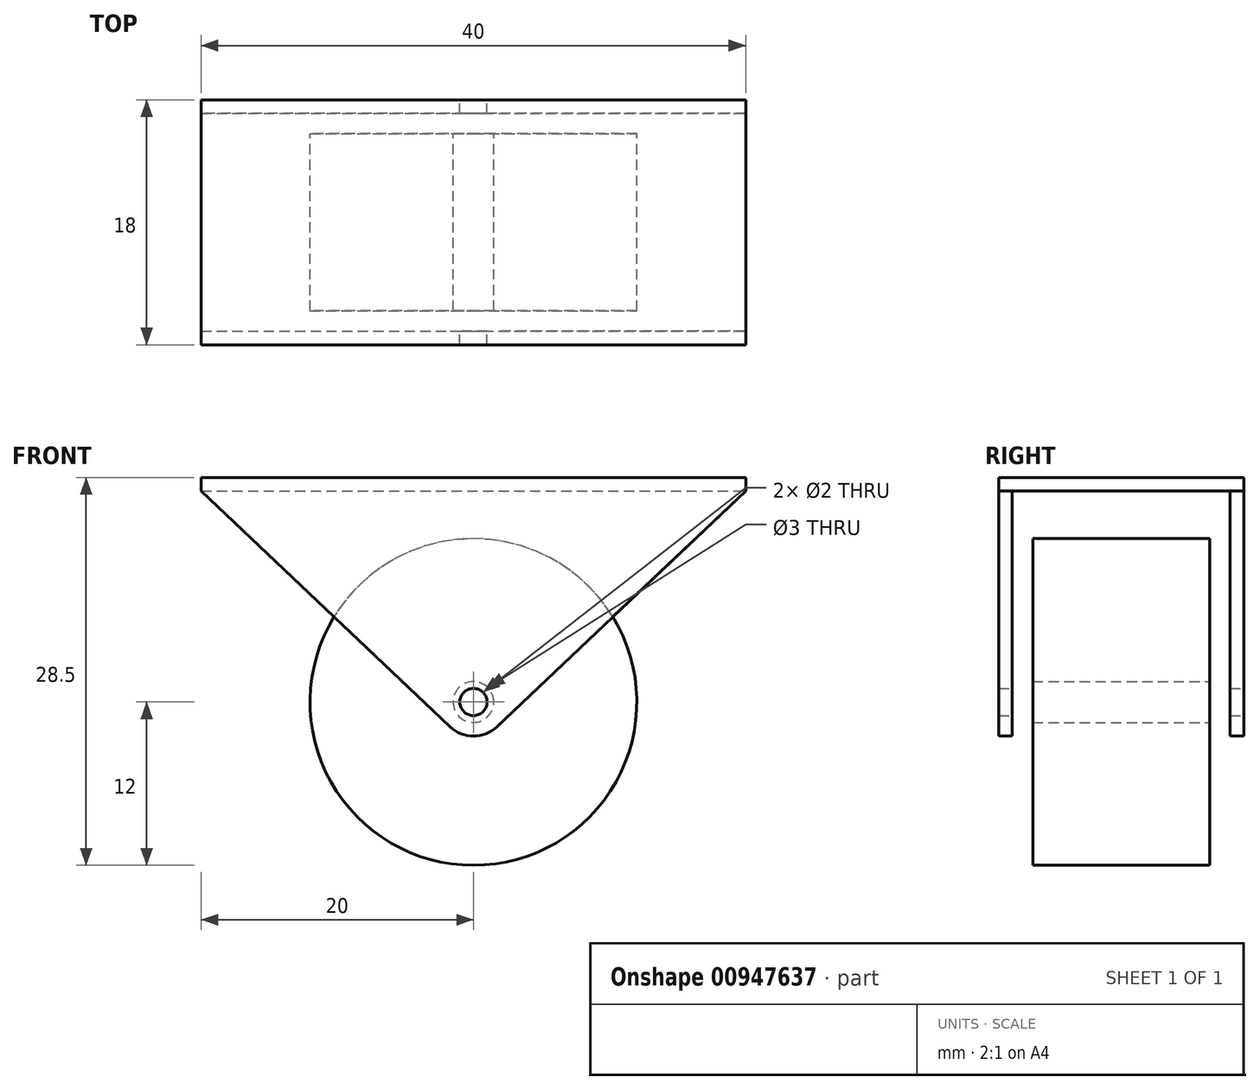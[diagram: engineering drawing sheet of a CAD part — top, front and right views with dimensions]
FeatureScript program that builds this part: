
annotation { "Feature Type Name" : "Feature", "Feature Type Description" : "" }
export const myFeature = defineFeature(function(context is Context, id is Id, definition is map)
    precondition{}
    {
        {
            var Q0;
            Q0=qCreatedBy(makeId("Front.planeOp"),FACE);
            var sketch = newSketch(context, id + "F0", { "sketchPlane" : qUnion([Q0])});
            skCircle(sketch, "E0", {"center": v(0, 0) * mm, "radius": 12 * mm});
            skCircle(sketch, "E1", {"center": v(0, 0) * mm, "radius": 1.5 * mm});
            skSolve(sketch);
        }
        {
            var Q0;
            Q0 = qSketchRegion(id + "F0", true);
            extrude(context, id + "F1", {"entities" : qUnion([Q0]), "depth" : 6.5 * mm, "offsetDistance" : 25 * mm, "hasSecondDirection" : true, "secondDirectionOppositeDirection" : true, "secondDirectionDepth" : 6.5 * mm});
        }
        {
            var Q0;
            Q0=qCreatedBy(makeId("Top.planeOp"),FACE);
            cPlane(context, id + "F2", {"entities" : qUnion([Q0]), "cplaneType" : CPlaneType.OFFSET, "offset" : (28 - 11.5) * mm, "width" : 150 * mm, "height" : 150 * mm});
        }
        {
            var Q0;
            Q0=qCreatedBy(id+"F2.planeOp",FACE);
            var sketch = newSketch(context, id + "F3", { "sketchPlane" : qUnion([Q0])});
            skLineSegment(sketch, "E2.bottom", {"start": v(-20, 9) * mm, "end": v(20, 9) * mm});
            skLineSegment(sketch, "E2.top", {"start": v(-20, -9) * mm, "end": v(20, -9) * mm});
            skLineSegment(sketch, "E2.left", {"start": v(-20, 9) * mm, "end": v(-20, -9) * mm});
            skLineSegment(sketch, "E2.right", {"start": v(20, 9) * mm, "end": v(20, -9) * mm});
            skPoint(sketch, "E3", {"position": v(-20, 0) * mm});
            skPoint(sketch, "E4", {"position": v(0, -9) * mm});
            skSolve(sketch);
        }
        {
            var Q0;
            Q0 = qSketchRegion(id + "F3", true);
            extrude(context, id + "F4", {"entities" : qUnion([Q0]), "oppositeDirection" : true, "depth" : 1 * mm, "offsetDistance" : 25 * mm});
        }
        {
            var Q0;
            Q0=makeQuery(id+"F4.opExtrude","SWEPT_FACE",FACE,{"disambiguationData":[OSD([sQuery(id+"F3.wireOp",EDGE,"E2.top")])]});
            var sketch = newSketch(context, id + "F5", { "sketchPlane" : qUnion([Q0])});
            skCircle(sketch, "E5", {"center": v(0, 0) * mm, "radius": 2.5 * mm});
            skLineSegment(sketch, "E6", {"start": v(-20, 15.5) * mm, "end": v(-1.72, -1.82) * mm});
            skLineSegment(sketch, "E7", {"start": v(20, 15.5) * mm, "end": v(1.72, -1.82) * mm});
            skSolve(sketch);
        }
        {
            var Q0;
            {var subQ0=sQuery(id+"F5.wireOp",EDGE,"E6");Q0=makeQuery(id+"F5.imprint","IMPRINT",FACE,{"disambiguationData":[TD([[makeQuery(id+"F5.imprint","IMPRINT",EDGE,{"derivedFrom":subQ0}),1.0]])]});}
            var Q1;
            {var subQ0=sQuery(id+"F5.wireOp",EDGE,"E5");var subQ1=makeQuery(id+"F5.imprint","INTERSECT",VERTEX,{"derivedFrom":[subQ0,sQuery(id+"F5.wireOp",EDGE,"E6")]});Q1=makeQuery(id+"F5.imprint","IMPRINT",FACE,{"disambiguationData":[TD([[makeQuery(id+"F5.imprint","IMPRINT",EDGE,{"disambiguationData":[TD([[subQ1,-1.0]])],"derivedFrom":subQ0}),1.0]])]});}
            extrude(context, id + "F6", {"entities" : qUnion([Q0, Q1]), "operationType" : NewBodyOperationType.ADD, "oppositeDirection" : true, "depth" : 1 * mm, "offsetDistance" : 25 * mm});
        }
        {
            var Q0;
            Q0=makeQuery(id+"F4.opExtrude","SWEPT_FACE",FACE,{"disambiguationData":[OSD([sQuery(id+"F3.wireOp",EDGE,"E2.bottom")])]});
            var sketch = newSketch(context, id + "F7", { "sketchPlane" : qUnion([Q0])});
            skLineSegment(sketch, "E8.0.0", {"start": v(1.72, -1.82) * mm, "end": v(20, 15.5) * mm});
            skLineSegment(sketch, "E8.0.1", {"start": v(20, 15.5) * mm, "end": v(-20, 15.5) * mm});
            skLineSegment(sketch, "E8.0.2", {"start": v(-20, 15.5) * mm, "end": v(-1.72, -1.82) * mm});
            skArc(sketch, "E8.0.3", {"start": v(-1.72, -1.82) * mm, "mid": v(0, -2.5) * mm, "end": v(1.72, -1.82) * mm});
            skSolve(sketch);
        }
        {
            var Q0;
            Q0 = qSketchRegion(id + "F7", true);
            extrude(context, id + "F8", {"entities" : qUnion([Q0]), "operationType" : NewBodyOperationType.ADD, "oppositeDirection" : true, "depth" : 1 * mm, "offsetDistance" : 25 * mm});
        }
        {
            var Q0;
            Q0=makeQuery(id+"F8.boolean.opBoolean","MERGE",FACE,{"derivedFrom":[makeQuery(id+"F4.opExtrude","SWEPT_FACE",FACE,{"disambiguationData":[OSD([sQuery(id+"F3.wireOp",EDGE,"E2.bottom")])]}),makeQuery(id+"F8.opExtrude","CAP_FACE",FACE,{"disambiguationData":[OSD([sQuery(id+"F7.wireOp",EDGE,"E8.0.0"),sQuery(id+"F7.wireOp",EDGE,"E8.0.1"),sQuery(id+"F7.wireOp",EDGE,"E8.0.2"),sQuery(id+"F7.wireOp",EDGE,"E8.0.3")])],"isStart":true})]});
            var sketch = newSketch(context, id + "F9", { "sketchPlane" : qUnion([Q0])});
            skCircle(sketch, "E9", {"center": v(0, 0) * mm, "radius": 1 * mm});
            skSolve(sketch);
        }
        {
            var Q0;
            Q0 = qSketchRegion(id + "F9", true);
            extrude(context, id + "F10", {"entities" : qUnion([Q0]), "operationType" : NewBodyOperationType.REMOVE, "endBound" : BoundingType.THROUGH_ALL, "oppositeDirection" : true, "depth" : 25 * mm, "offsetDistance" : 25 * mm});
        }
    });
